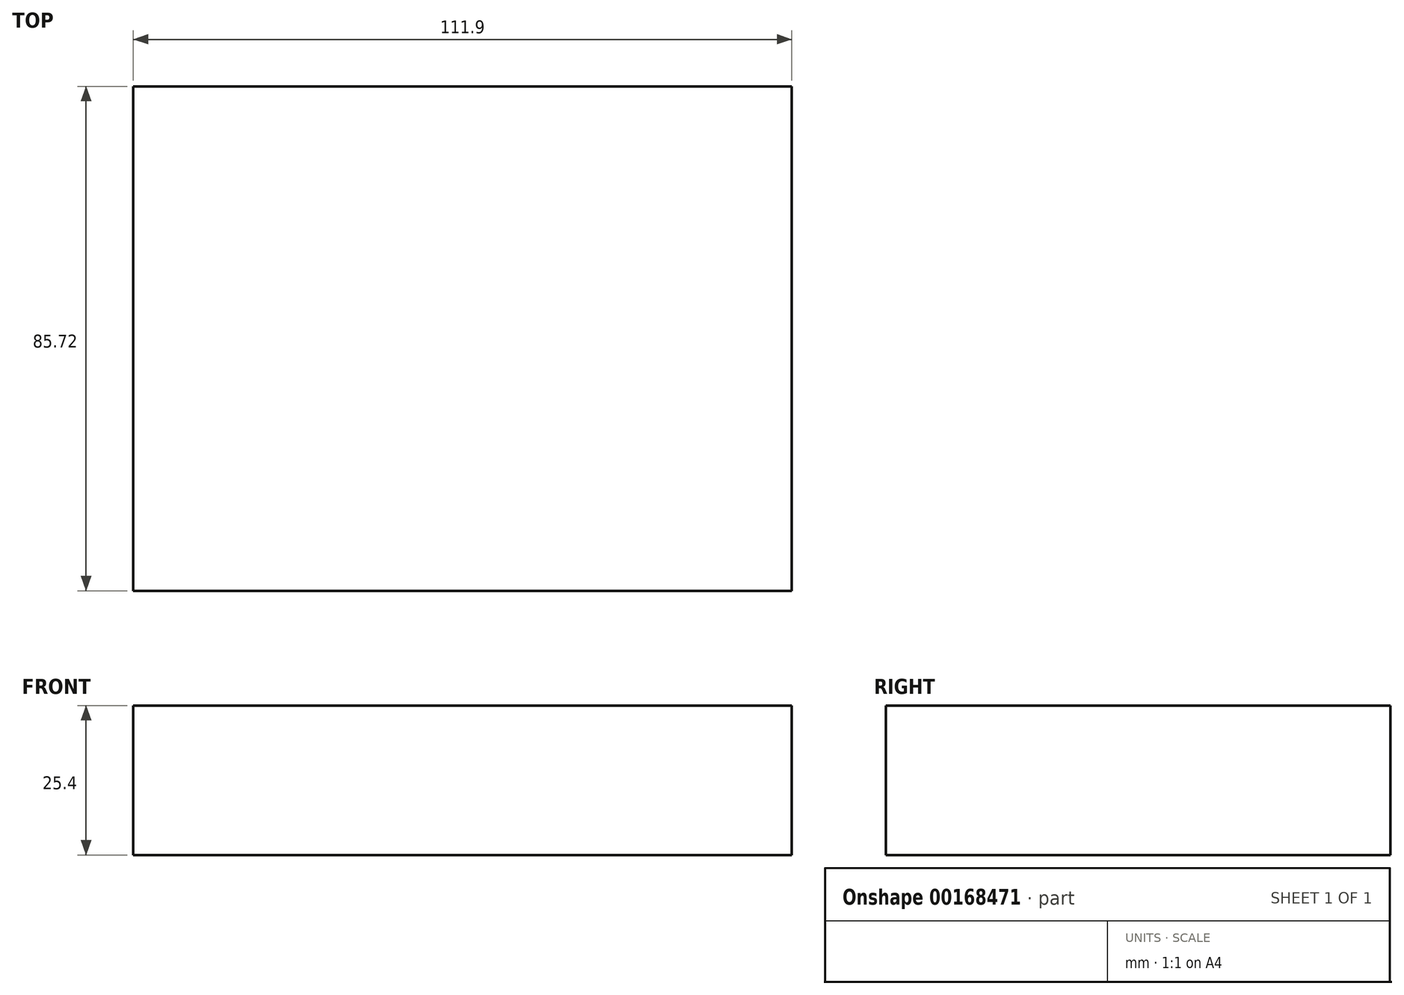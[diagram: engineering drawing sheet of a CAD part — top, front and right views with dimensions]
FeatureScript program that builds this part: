
annotation { "Feature Type Name" : "Feature", "Feature Type Description" : "" }
export const myFeature = defineFeature(function(context is Context, id is Id, definition is map)
    precondition{}
    {
        {
            var Q0;
            Q0=qCreatedBy(makeId("Top.planeOp"),FACE);
            var sketch = newSketch(context, id + "F0", { "sketchPlane" : qUnion([Q0])});
            skLineSegment(sketch, "E0.bottom", {"start": v(-70.97, 56.67) * mm, "end": v(40.93, 56.67) * mm});
            skLineSegment(sketch, "E0.top", {"start": v(-70.97, -29.05) * mm, "end": v(40.93, -29.05) * mm});
            skLineSegment(sketch, "E0.left", {"start": v(-70.97, 56.67) * mm, "end": v(-70.97, -29.05) * mm});
            skLineSegment(sketch, "E0.right", {"start": v(40.93, 56.67) * mm, "end": v(40.93, -29.05) * mm});
            skSolve(sketch);
        }
        {
            var Q0;
            Q0=makeQuery(id+"F0.imprint","IMPRINT",FACE,{"disambiguationData":[TD([[makeQuery(id+"F0.imprint","IMPRINT",EDGE,{"derivedFrom":sQuery(id+"F0.wireOp",EDGE,"E0.bottom")}),-1.0]])]});
            extrude(context, id + "F1", {"entities" : qUnion([Q0]), "depth" : 25.4 * mm});
        }
    });
